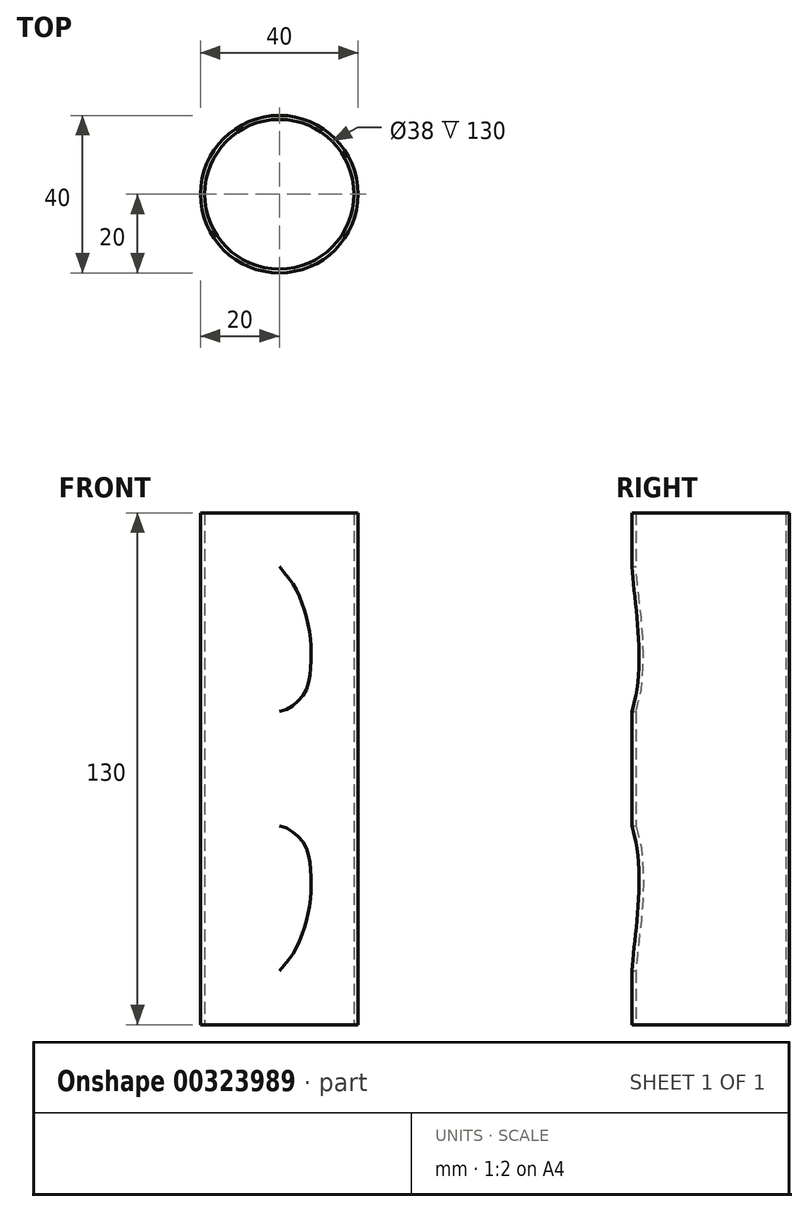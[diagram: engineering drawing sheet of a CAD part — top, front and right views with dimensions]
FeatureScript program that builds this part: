
annotation { "Feature Type Name" : "Feature", "Feature Type Description" : "" }
export const myFeature = defineFeature(function(context is Context, id is Id, definition is map)
    precondition{}
    {
        {
            var Q0;
            Q0=qCreatedBy(makeId("Top.planeOp"),FACE);
            var sketch = newSketch(context, id + "F0", { "sketchPlane" : qUnion([Q0])});
            skCircle(sketch, "E0", {"center": v(0, 0) * mm, "radius": 20 * mm});
            skCircle(sketch, "E1", {"center": v(0, 0) * mm, "radius": 19 * mm});
            skSolve(sketch);
        }
        {
            var Q0;
            Q0=makeQuery(id+"F0.imprint","IMPRINT",FACE,{"disambiguationData":[TD([[makeQuery(id+"F0.imprint","IMPRINT",EDGE,{"derivedFrom":sQuery(id+"F0.wireOp",EDGE,"E0")}),1.0]])]});
            extrude(context, id + "F1", {"entities" : qUnion([Q0]), "depth" : 65 * mm});
        }
        {
            var Q0;
            Q0=qCreatedBy(makeId("Front.planeOp"),FACE);
            var sketch = newSketch(context, id + "F2", { "sketchPlane" : qUnion([Q0])});
            skPoint(sketch, "E2", {"position": v(0, 51.35) * mm});
            skPoint(sketch, "E3", {"position": v(0, 14.56) * mm});
            skFitSpline(sketch, "E4", {"points": [v(0, 14.56) * mm, v(5.42, 17.85) * mm, v(7.68, 23.13) * mm, v(7.46, 35.95) * mm, v(3.35, 47.14) * mm, v(0, 51.35) * mm], "startDerivative": vector(32.42, 2.75) * mm, "endDerivative": vector(-22.48, 28.95) * mm});
            skFitSpline(sketch, "E5.MirrorCS", {"points": [v(0, 14.56) * mm, v(-5.42, 17.85) * mm, v(-7.68, 23.13) * mm, v(-7.46, 35.95) * mm, v(-3.35, 47.14) * mm, v(0, 51.35) * mm], "startDerivative": vector(-32.42, 2.75) * mm, "endDerivative": vector(22.48, 28.95) * mm});
            skSolve(sketch);
        }
        {
            var Q0;
            Q0 = qSketchRegion(id + "F2", true);
            extrude(context, id + "F3", {"entities" : qUnion([Q0]), "operationType" : NewBodyOperationType.REMOVE, "depth" : 41.1 * mm});
        }
        {
            var Q0;
            Q0=makeQuery(id+"F1.opExtrude","SWEPT_BODY",BODY,{"disambiguationData":[OSD([sQuery(id+"F0.wireOp",EDGE,"E0"),sQuery(id+"F0.wireOp",EDGE,"E1")])]});
            var Q1;
            Q1=qCreatedBy(makeId("Top.planeOp"),FACE);
            mirror(context, id + "F4", {"operationType" : NewBodyOperationType.ADD, "entities" : qUnion([Q0]), "mirrorPlane" : qUnion([Q1])});
        }
    });
